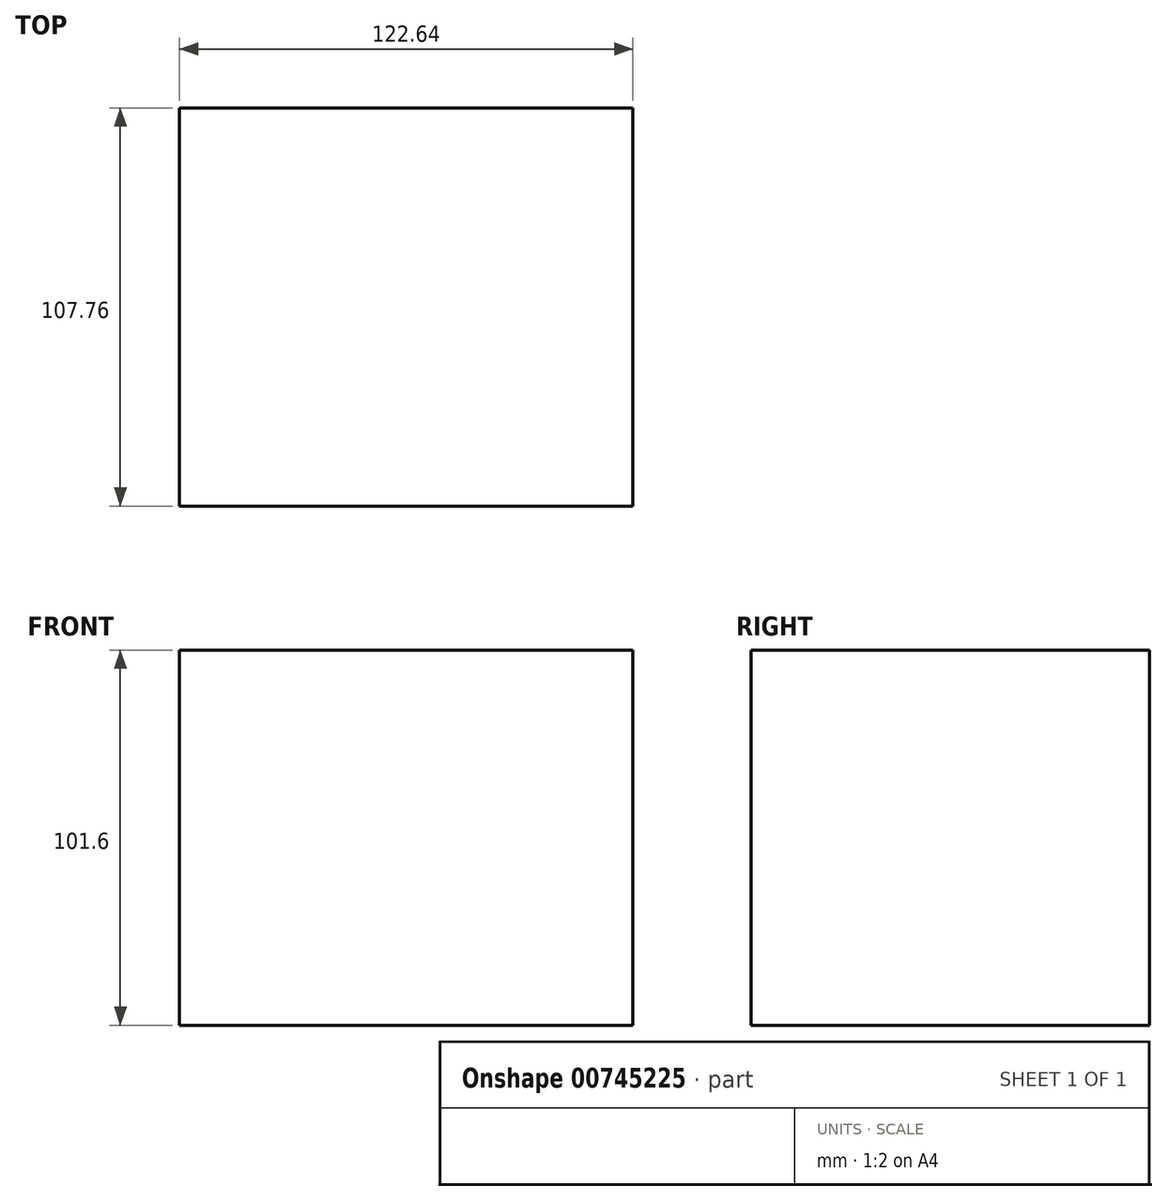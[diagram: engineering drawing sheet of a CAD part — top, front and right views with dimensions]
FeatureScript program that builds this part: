
annotation { "Feature Type Name" : "Feature", "Feature Type Description" : "" }
export const myFeature = defineFeature(function(context is Context, id is Id, definition is map)
    precondition{}
    {
        {
            var Q0;
            Q0=qCreatedBy(makeId("Top.planeOp"),FACE);
            var sketch = newSketch(context, id + "F0", { "sketchPlane" : qUnion([Q0])});
            skLineSegment(sketch, "E0.bottom", {"start": v(-59.4, -49) * mm, "end": v(63.23, -49) * mm});
            skLineSegment(sketch, "E0.top", {"start": v(-59.4, 58.76) * mm, "end": v(63.23, 58.76) * mm});
            skLineSegment(sketch, "E0.left", {"start": v(-59.4, -49) * mm, "end": v(-59.4, 58.76) * mm});
            skLineSegment(sketch, "E0.right", {"start": v(63.23, -49) * mm, "end": v(63.23, 58.76) * mm});
            skSolve(sketch);
        }
        {
            var Q0;
            Q0 = qSketchRegion(id + "F0", true);
            extrude(context, id + "F1", {"entities" : qUnion([Q0]), "depth" : 101.6 * mm, "offsetDistance" : 25.4 * mm});
        }
        {
            var Q0;
            Q0=makeQuery(id+"F1.opExtrude","CAP_FACE",FACE,{"disambiguationData":[OSD([sQuery(id+"F0.wireOp",EDGE,"E0.bottom"),sQuery(id+"F0.wireOp",EDGE,"E0.top"),sQuery(id+"F0.wireOp",EDGE,"E0.left"),sQuery(id+"F0.wireOp",EDGE,"E0.right")])],"isStart":false});
            var sketch = newSketch(context, id + "F2", { "sketchPlane" : qUnion([Q0])});
            skCircle(sketch, "E1", {"center": v(-49.42, 49.66) * mm, "radius": 5.81 * mm});
            skSolve(sketch);
        }
        {
            var Q0;
            Q0=makeQuery(id+"F2.imprint","IMPRINT",FACE,{"disambiguationData":[TD([[makeQuery(id+"F2.imprint","IMPRINT",EDGE,{"derivedFrom":sQuery(id+"F2.wireOp",EDGE,"E1")}),1.0]])]});
            extrude(context, id + "F3", {"entities" : qUnion([Q0]), "operationType" : NewBodyOperationType.ADD, "depth" : -101.6 * mm, "offsetDistance" : 25.4 * mm});
        }
    });
